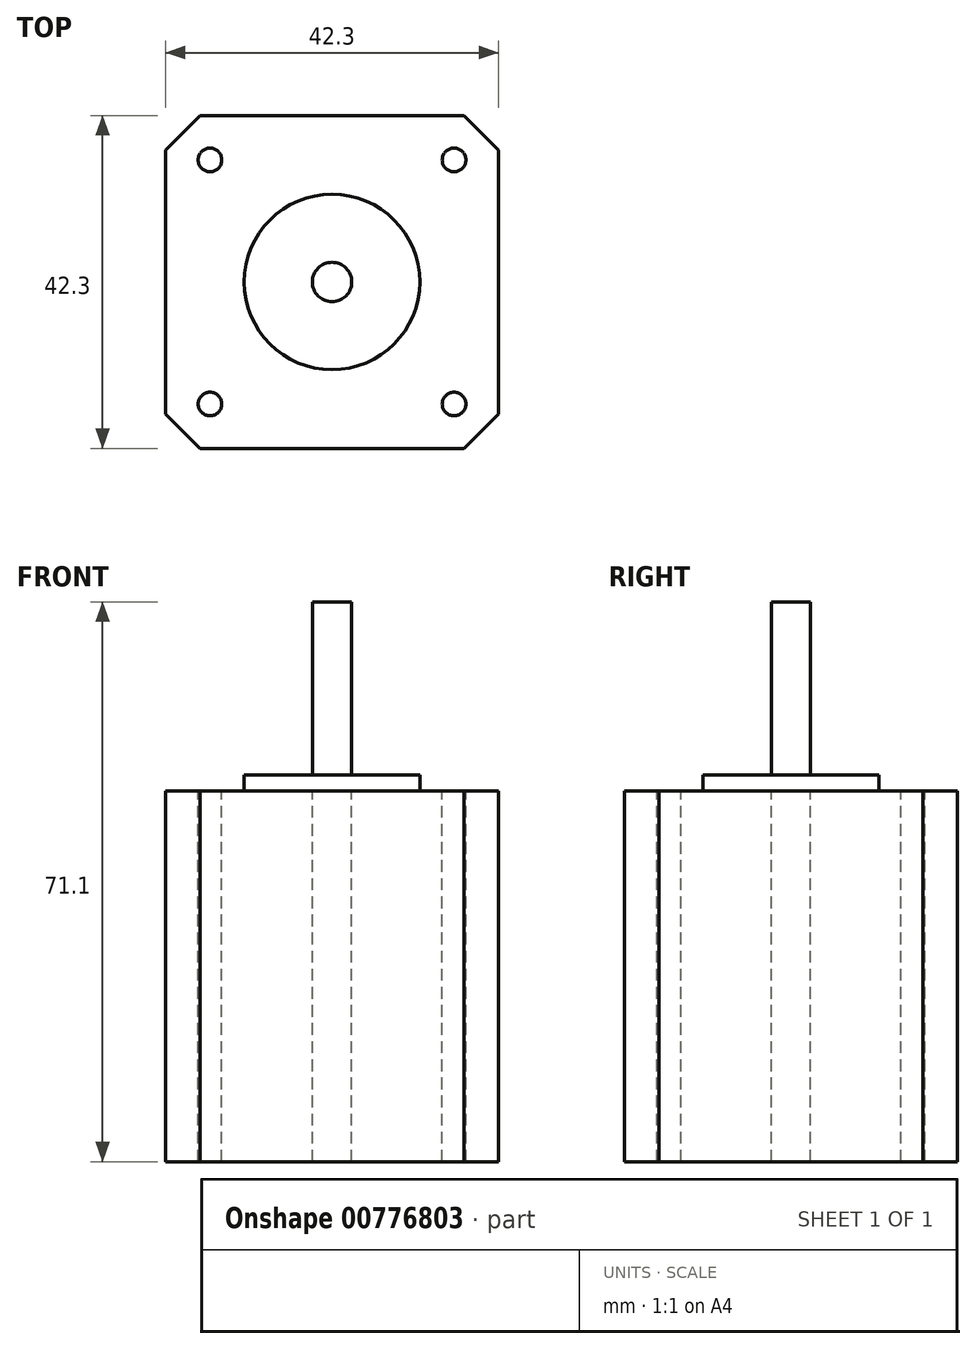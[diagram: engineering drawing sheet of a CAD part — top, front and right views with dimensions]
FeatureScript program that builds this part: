
annotation { "Feature Type Name" : "Feature", "Feature Type Description" : "" }
export const myFeature = defineFeature(function(context is Context, id is Id, definition is map)
    precondition{}
    {
        {
            var Q0;
            Q0=qCreatedBy(makeId("Top.planeOp"),FACE);
            var sketch = newSketch(context, id + "F0", { "sketchPlane" : qUnion([Q0])});
            skLineSegment(sketch, "E0.bottom", {"start": v(21.15, -21.15) * mm, "end": v(-21.15, -21.15) * mm, "construction": true});
            skLineSegment(sketch, "E0.top", {"start": v(21.15, 21.15) * mm, "end": v(-21.15, 21.15) * mm, "construction": true});
            skLineSegment(sketch, "E0.left", {"start": v(21.15, -21.15) * mm, "end": v(21.15, 21.15) * mm, "construction": true});
            skLineSegment(sketch, "E0.right", {"start": v(-21.15, -21.15) * mm, "end": v(-21.15, 21.15) * mm, "construction": true});
            skPoint(sketch, "E0.middle", {"position": v(0, 0) * mm});
            skLineSegment(sketch, "E1", {"start": v(-21.15, 16.75) * mm, "end": v(-21.15, -16.75) * mm});
            skPoint(sketch, "E2", {"position": v(-21.15, 0) * mm});
            skLineSegment(sketch, "E3", {"start": v(0, 21.15) * mm, "end": v(0, -21.15) * mm, "construction": true});
            skLineSegment(sketch, "E4.MirrorCS", {"start": v(21.15, 16.75) * mm, "end": v(21.15, -16.75) * mm});
            skLineSegment(sketch, "E5", {"start": v(-16.75, 21.15) * mm, "end": v(16.75, 21.15) * mm});
            skPoint(sketch, "E6", {"position": v(0, 21.15) * mm});
            skLineSegment(sketch, "E7", {"start": v(-21.15, 0) * mm, "end": v(21.15, 0) * mm, "construction": true});
            skLineSegment(sketch, "E8.MirrorCS", {"start": v(-16.75, -21.15) * mm, "end": v(16.75, -21.15) * mm});
            skLineSegment(sketch, "E9", {"start": v(-21.15, 16.75) * mm, "end": v(-16.75, 21.15) * mm});
            skLineSegment(sketch, "E10", {"start": v(16.75, 21.15) * mm, "end": v(21.15, 16.75) * mm});
            skLineSegment(sketch, "E11", {"start": v(21.15, -16.75) * mm, "end": v(16.75, -21.15) * mm});
            skLineSegment(sketch, "E12", {"start": v(-16.75, -21.15) * mm, "end": v(-21.15, -16.75) * mm});
            skCircle(sketch, "E13", {"center": v(0, 0) * mm, "radius": 11.15 * mm});
            skCircle(sketch, "E14", {"center": v(0, 0) * mm, "radius": 2.5 * mm});
            skCircle(sketch, "E15", {"center": v(15.5, 15.5) * mm, "radius": 1.5 * mm});
            skCircle(sketch, "E16.MirrorC", {"center": v(15.5, -15.5) * mm, "radius": 1.5 * mm});
            skCircle(sketch, "E17.MirrorC", {"center": v(-15.5, 15.5) * mm, "radius": 1.5 * mm});
            skCircle(sketch, "E18.MirrorC", {"center": v(-15.5, -15.5) * mm, "radius": 1.5 * mm});
            skLineSegment(sketch, "E19", {"start": v(-15.5, 15.5) * mm, "end": v(15.5, 15.5) * mm, "construction": true});
            skLineSegment(sketch, "E20", {"start": v(-15.5, 15.5) * mm, "end": v(-15.5, -15.5) * mm, "construction": true});
            skSolve(sketch);
        }
        {
            var Q0;
            Q0=qSketchRegion(id+"F0",true);
            var Q1;
            Q1=makeQuery(id+"F0.imprint","IMPRINT",FACE,{"disambiguationData":[TD([[makeQuery(id+"F0.imprint","IMPRINT",EDGE,{"derivedFrom":sQuery(id+"F0.wireOp",EDGE,"E13")}),1.0]])]});
            extrude(context, id + "F1", {"entities" : qUnion([Q0, Q1]), "oppositeDirection" : true, "depth" : 47.1 * mm});
        }
        {
            var Q0;
            Q0=makeQuery(id+"F0.imprint","IMPRINT",FACE,{"disambiguationData":[TD([[makeQuery(id+"F0.imprint","IMPRINT",EDGE,{"derivedFrom":sQuery(id+"F0.wireOp",EDGE,"E13")}),1.0]])]});
            extrude(context, id + "F2", {"entities" : qUnion([Q0]), "operationType" : NewBodyOperationType.ADD, "depth" : 2 * mm});
        }
        {
            var Q0;
            Q0=makeQuery(id+"F0.imprint","IMPRINT",FACE,{"disambiguationData":[TD([[makeQuery(id+"F0.imprint","IMPRINT",EDGE,{"derivedFrom":sQuery(id+"F0.wireOp",EDGE,"E14")}),1.0]])]});
            extrude(context, id + "F3", {"entities" : qUnion([Q0]), "operationType" : NewBodyOperationType.ADD, "depth" : 24 * mm});
        }
    });
